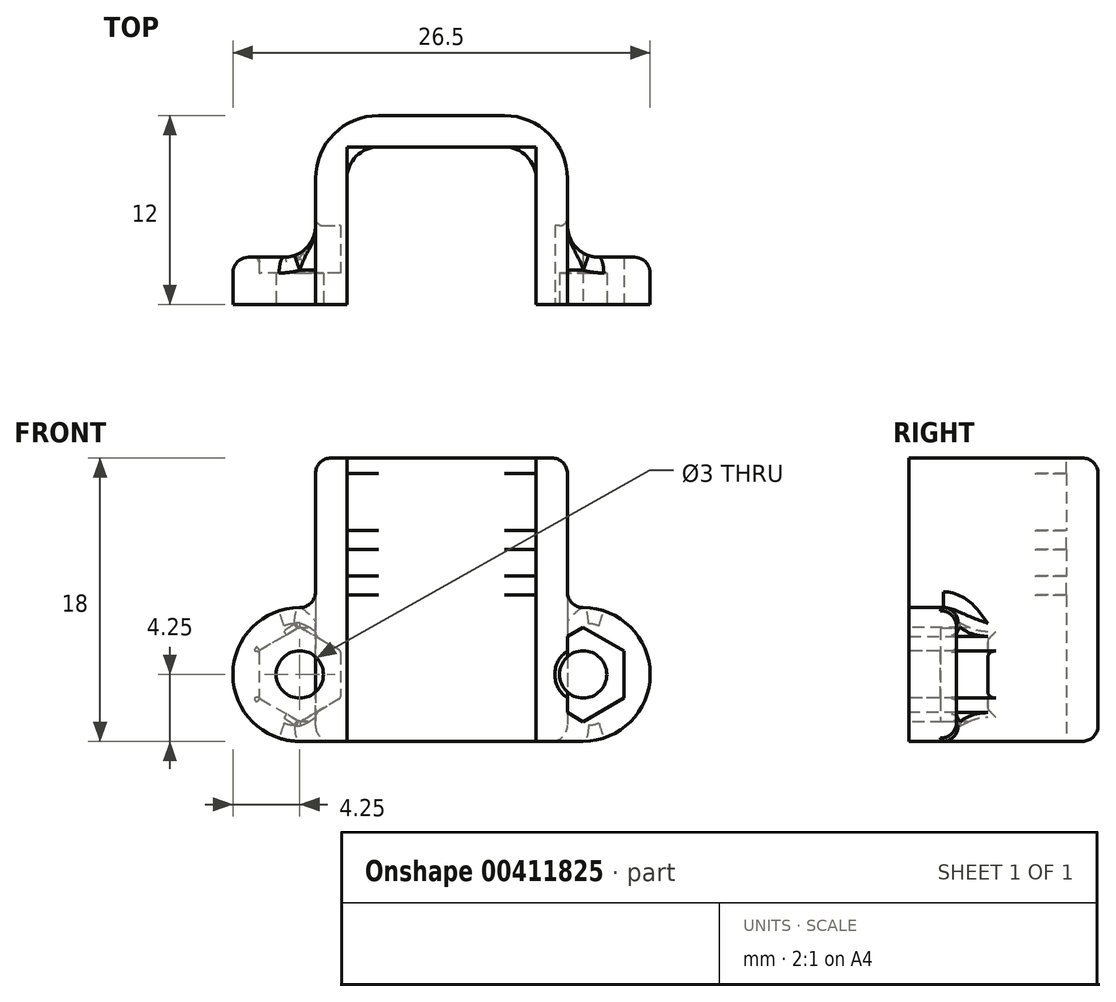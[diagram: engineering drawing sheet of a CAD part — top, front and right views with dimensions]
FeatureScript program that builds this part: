
annotation { "Feature Type Name" : "Feature", "Feature Type Description" : "" }
export const myFeature = defineFeature(function(context is Context, id is Id, definition is map)
    precondition{}
    {
        {
            var Q0;
            Q0=qCreatedBy(makeId("Top.planeOp"),FACE);
            var sketch = newSketch(context, id + "F0", { "sketchPlane" : qUnion([Q0])});
            skLineSegment(sketch, "E0", {"start": v(0, 0) * mm, "end": v(0, 8) * mm});
            skLineSegment(sketch, "E1", {"start": v(2, 10) * mm, "end": v(10, 10) * mm});
            skLineSegment(sketch, "E2", {"start": v(12, 8) * mm, "end": v(12, 0) * mm});
            skLineSegment(sketch, "E3", {"start": v(12, 0) * mm, "end": v(0, 0) * mm, "construction": true});
            skPoint(sketch, "E4.visualSharp", {"position": v(0, 10) * mm});
            skArc(sketch, "E4.filletArc", {"start": v(2, 10) * mm, "mid": v(0.59, 9.41) * mm, "end": v(0, 8) * mm});
            skPoint(sketch, "E5.visualSharp", {"position": v(12, 10) * mm});
            skArc(sketch, "E5.filletArc", {"start": v(12, 8) * mm, "mid": v(11.41, 9.41) * mm, "end": v(10, 10) * mm});
            skLineSegment(sketch, "E6.0", {"start": v(-2, 0) * mm, "end": v(-2, 8) * mm});
            skLineSegment(sketch, "E6.1", {"start": v(14, 8) * mm, "end": v(14, 0) * mm});
            skArc(sketch, "E6.2", {"start": v(14, 8) * mm, "mid": v(12.83, 10.83) * mm, "end": v(10, 12) * mm});
            skLineSegment(sketch, "E6.3", {"start": v(2, 12) * mm, "end": v(10, 12) * mm});
            skArc(sketch, "E6.4", {"start": v(2, 12) * mm, "mid": v(-0.83, 10.83) * mm, "end": v(-2, 8) * mm});
            skLineSegment(sketch, "E7", {"start": v(-2, 0) * mm, "end": v(0, 0) * mm});
            skLineSegment(sketch, "E8", {"start": v(12, 0) * mm, "end": v(14, 0) * mm});
            skSolve(sketch);
        }
        {
            var Q0;
            Q0 = qSketchRegion(id + "F0", true);
            extrude(context, id + "F1", {"entities" : qUnion([Q0]), "depth" : 18 * mm});
        }
        {
            var Q0;
            Q0=qCreatedBy(makeId("Front.planeOp"),FACE);
            var sketch = newSketch(context, id + "F2", { "sketchPlane" : qUnion([Q0])});
            skCircle(sketch, "E9", {"center": v(-3, 4.25) * mm, "radius": 1.8 * mm});
            skCircle(sketch, "E10", {"center": v(-3, 4.25) * mm, "radius": 1.5 * mm});
            skLineSegment(sketch, "E11.bottom", {"start": v(1.25, 8.5) * mm, "end": v(-3, 8.5) * mm, "construction": true});
            skLineSegment(sketch, "E11.top", {"start": v(1.25, 0) * mm, "end": v(-3, 0) * mm, "construction": true});
            skLineSegment(sketch, "E11.left", {"start": v(1.25, 8.5) * mm, "end": v(1.25, 0) * mm, "construction": true});
            skLineSegment(sketch, "E11.right", {"start": v(-7.25, 8.5) * mm, "end": v(-7.25, 0) * mm, "construction": true});
            skLineSegment(sketch, "E12", {"start": v(6, 0) * mm, "end": v(6, 18.17) * mm, "construction": true});
            skLineSegment(sketch, "E13", {"start": v(-3, 0) * mm, "end": v(-7.25, 0) * mm, "construction": true});
            skLineSegment(sketch, "E14", {"start": v(-3, 8.5) * mm, "end": v(-7.25, 8.5) * mm, "construction": true});
            skArc(sketch, "E15", {"start": v(-3, 8.5) * mm, "mid": v(-7.25, 4.25) * mm, "end": v(-3, 0) * mm});
            skArc(sketch, "E16", {"start": v(-3, 0) * mm, "mid": v(1.25, 4.25) * mm, "end": v(-3, 8.5) * mm, "construction": true});
            skLineSegment(sketch, "E17", {"start": v(-3, 0) * mm, "end": v(0, 0) * mm});
            skLineSegment(sketch, "E18", {"start": v(0, 0) * mm, "end": v(0, 8.5) * mm});
            skLineSegment(sketch, "E19", {"start": v(0, 8.5) * mm, "end": v(-3, 8.5) * mm});
            skLineSegment(sketch, "E20.MirrorCS", {"start": v(15, 0) * mm, "end": v(12, 0) * mm});
            skLineSegment(sketch, "E21.MirrorCS", {"start": v(12, 8.5) * mm, "end": v(15, 8.5) * mm});
            skCircle(sketch, "E22.MirrorC", {"center": v(15, 4.25) * mm, "radius": 1.5 * mm});
            skCircle(sketch, "E23.MirrorC", {"center": v(15, 4.25) * mm, "radius": 1.8 * mm});
            skLineSegment(sketch, "E24.MirrorCS", {"start": v(10.75, 8.5) * mm, "end": v(10.75, 0) * mm, "construction": true});
            skLineSegment(sketch, "E25.MirrorCS", {"start": v(15, 8.5) * mm, "end": v(19.25, 8.5) * mm, "construction": true});
            skLineSegment(sketch, "E26.MirrorCS", {"start": v(10.75, 0) * mm, "end": v(15, 0) * mm, "construction": true});
            skArc(sketch, "E27.MirrorCS", {"start": v(15, 0) * mm, "mid": v(10.75, 4.25) * mm, "end": v(15, 8.5) * mm, "construction": true});
            skLineSegment(sketch, "E28.MirrorCS", {"start": v(10.75, 8.5) * mm, "end": v(15, 8.5) * mm, "construction": true});
            skLineSegment(sketch, "E29.MirrorCS", {"start": v(19.25, 8.5) * mm, "end": v(19.25, 0) * mm, "construction": true});
            skLineSegment(sketch, "E30.MirrorCS", {"start": v(15, 0) * mm, "end": v(19.25, 0) * mm, "construction": true});
            skLineSegment(sketch, "E31.MirrorCS", {"start": v(12, 0) * mm, "end": v(12, 8.5) * mm});
            skArc(sketch, "E32.MirrorCS", {"start": v(15, 8.5) * mm, "mid": v(19.25, 4.25) * mm, "end": v(15, 0) * mm});
            skCircle(sketch, "E33", {"center": v(15, 4.25) * mm, "radius": 3 * mm, "construction": true});
            skLineSegment(sketch, "E34.0", {"start": v(17.6, 5.75) * mm, "end": v(17.6, 2.75) * mm});
            skLineSegment(sketch, "E34.1", {"start": v(17.6, 2.75) * mm, "end": v(15, 1.25) * mm});
            skLineSegment(sketch, "E34.2", {"start": v(15, 1.25) * mm, "end": v(12.4, 2.75) * mm});
            skLineSegment(sketch, "E34.3", {"start": v(12.4, 2.75) * mm, "end": v(12.4, 5.75) * mm});
            skLineSegment(sketch, "E34.4", {"start": v(12.4, 5.75) * mm, "end": v(15, 7.25) * mm});
            skLineSegment(sketch, "E34.5", {"start": v(15, 7.25) * mm, "end": v(17.6, 5.75) * mm});
            skLineSegment(sketch, "E35.MirrorCS", {"start": v(-5.6, 5.75) * mm, "end": v(-5.6, 2.75) * mm});
            skLineSegment(sketch, "E36.MirrorCS", {"start": v(-3, 7.25) * mm, "end": v(-5.6, 5.75) * mm});
            skLineSegment(sketch, "E37.MirrorCS", {"start": v(-0.4, 5.75) * mm, "end": v(-3, 7.25) * mm});
            skLineSegment(sketch, "E38.MirrorCS", {"start": v(-0.4, 2.75) * mm, "end": v(-0.4, 5.75) * mm});
            skLineSegment(sketch, "E39.MirrorCS", {"start": v(-3, 1.25) * mm, "end": v(-0.4, 2.75) * mm});
            skLineSegment(sketch, "E40.MirrorCS", {"start": v(-5.6, 2.75) * mm, "end": v(-3, 1.25) * mm});
            skSolve(sketch);
        }
        {
            var Q0;
            Q0=makeQuery(id+"F2.imprint","IMPRINT",FACE,{"disambiguationData":[TD([[makeQuery(id+"F2.imprint","IMPRINT",EDGE,{"derivedFrom":sQuery(id+"F2.wireOp",EDGE,"E9")}),-1.0]])]});
            var Q1;
            Q1=makeQuery(id+"F2.imprint","IMPRINT",FACE,{"disambiguationData":[TD([[makeQuery(id+"F2.imprint","IMPRINT",EDGE,{"derivedFrom":sQuery(id+"F2.wireOp",EDGE,"E9")}),1.0]])]});
            var Q2;
            Q2=makeQuery(id+"F2.imprint","IMPRINT",FACE,{"disambiguationData":[TD([[makeQuery(id+"F2.imprint","IMPRINT",EDGE,{"derivedFrom":sQuery(id+"F2.wireOp",EDGE,"E20.MirrorCS")}),-1.0]])]});
            var Q3;
            Q3=makeQuery(id+"F2.imprint","IMPRINT",FACE,{"disambiguationData":[TD([[makeQuery(id+"F2.imprint","IMPRINT",EDGE,{"derivedFrom":sQuery(id+"F2.wireOp",EDGE,"E22.MirrorC")}),1.0]])]});
            var Q4;
            Q4=makeQuery(id+"F2.imprint","IMPRINT",FACE,{"disambiguationData":[TD([[makeQuery(id+"F2.imprint","IMPRINT",EDGE,{"derivedFrom":sQuery(id+"F2.wireOp",EDGE,"E23.MirrorC")}),1.0]])]});
            var Q5;
            Q5=makeQuery(id+"F2.imprint","IMPRINT",FACE,{"disambiguationData":[TD([[makeQuery(id+"F2.imprint","IMPRINT",EDGE,{"derivedFrom":sQuery(id+"F2.wireOp",EDGE,"E15")}),1.0]])]});
            extrude(context, id + "F3", {"entities" : qUnion([Q0, Q1, Q2, Q3, Q4, Q5]), "operationType" : NewBodyOperationType.ADD, "oppositeDirection" : true, "depth" : 3 * mm});
        }
        {
            var Q0;
            Q0=makeQuery(id+"F2.imprint","IMPRINT",FACE,{"disambiguationData":[TD([[makeQuery(id+"F2.imprint","IMPRINT",EDGE,{"derivedFrom":sQuery(id+"F2.wireOp",EDGE,"E10")}),1.0]])]});
            var Q1;
            Q1=makeQuery(id+"F2.imprint","IMPRINT",FACE,{"disambiguationData":[TD([[makeQuery(id+"F2.imprint","IMPRINT",EDGE,{"derivedFrom":sQuery(id+"F2.wireOp",EDGE,"E22.MirrorC")}),-1.0]])]});
            var Q2;
            Q2=sQuery(id+"F2.wireOp",EDGE,"E10");
            extrude(context, id + "F4", {"entities" : qUnion([Q0, Q1]), "operationType" : NewBodyOperationType.REMOVE, "surfaceEntities" : qUnion([Q2]), "oppositeDirection" : true, "depth" : 5 * mm});
        }
        {
            var Q0;
            Q0=makeQuery(id+"F3.boolean.opBoolean","INTERSECT",EDGE,{"derivedFrom":[makeQuery(id+"F1.opExtrude","SWEPT_FACE",FACE,{"disambiguationData":[OSD([sQuery(id+"F0.wireOp",EDGE,"E6.1")])]}),makeQuery(id+"F3.opExtrude","CAP_FACE",FACE,{"disambiguationData":[OSD([sQuery(id+"F2.wireOp",EDGE,"E20.MirrorCS"),sQuery(id+"F2.wireOp",EDGE,"E21.MirrorCS"),sQuery(id+"F2.wireOp",EDGE,"E22.MirrorC"),sQuery(id+"F2.wireOp",EDGE,"E31.MirrorCS"),sQuery(id+"F2.wireOp",EDGE,"E32.MirrorCS")])],"isStart":false})]});
            var Q1;
            Q1=makeQuery(id+"F3.boolean.opBoolean","INTERSECT",EDGE,{"derivedFrom":[makeQuery(id+"F1.opExtrude","SWEPT_FACE",FACE,{"disambiguationData":[OSD([sQuery(id+"F0.wireOp",EDGE,"E6.0")])]}),makeQuery(id+"F3.opExtrude","CAP_FACE",FACE,{"disambiguationData":[OSD([sQuery(id+"F2.wireOp",EDGE,"E10"),sQuery(id+"F2.wireOp",EDGE,"E15"),sQuery(id+"F2.wireOp",EDGE,"E17"),sQuery(id+"F2.wireOp",EDGE,"E18"),sQuery(id+"F2.wireOp",EDGE,"E19")])],"isStart":false})]});
            fillet(context, id + "F5", {"entities" : qUnion([Q0, Q1]), "radius" : 2 * mm, "tangentPropagation" : true, "allowEdgeOverflow" : false});
        }
        {
            var Q0;
            Q0=makeQuery(id+"F3.opExtrude","CAP_EDGE",EDGE,{"disambiguationData":[OSD([sQuery(id+"F2.wireOp",EDGE,"E15")])],"isStart":false});
            var Q1;
            Q1=makeQuery(id+"F3.opExtrude","CAP_EDGE",EDGE,{"disambiguationData":[OSD([sQuery(id+"F2.wireOp",EDGE,"E32.MirrorCS")])],"isStart":false});
            fillet(context, id + "F6", {"entities" : qUnion([Q0, Q1]), "radius" : 1 * mm, "tangentPropagation" : true, "allowEdgeOverflow" : false});
        }
        {
            var Q0;
            Q0=makeQuery(id+"F1.opExtrude","CAP_EDGE",EDGE,{"disambiguationData":[OSD([sQuery(id+"F0.wireOp",EDGE,"E6.3")])],"isStart":false});
            var Q1;
            Q1=makeQuery(id+"F1.opExtrude","CAP_EDGE",EDGE,{"disambiguationData":[OSD([sQuery(id+"F0.wireOp",EDGE,"E6.2")])],"isStart":false});
            var Q2;
            Q2=makeQuery(id+"F1.opExtrude","CAP_EDGE",EDGE,{"disambiguationData":[OSD([sQuery(id+"F0.wireOp",EDGE,"E6.1")])],"isStart":false});
            var Q3;
            Q3=makeQuery(id+"F1.opExtrude","CAP_EDGE",EDGE,{"disambiguationData":[OSD([sQuery(id+"F0.wireOp",EDGE,"E6.4")])],"isStart":false});
            var Q4;
            Q4=makeQuery(id+"F1.opExtrude","CAP_EDGE",EDGE,{"disambiguationData":[OSD([sQuery(id+"F0.wireOp",EDGE,"E6.0")])],"isStart":false});
            fillet(context, id + "F7", {"entities" : qUnion([Q0, Q1, Q2, Q3, Q4]), "radius" : 1 * mm, "tangentPropagation" : true, "allowEdgeOverflow" : false});
        }
        {
            var Q0;
            {var subQ0=makeQuery(id+"F1.opExtrude","SWEPT_FACE",FACE,{"disambiguationData":[OSD([sQuery(id+"F0.wireOp",EDGE,"E6.1")])]});var subQ1=sQuery(id+"F2.wireOp",EDGE,"E21.MirrorCS");Q0=makeQuery(id+"F6.opFillet","BLEND_EDGE",EDGE,{"blendedFrom":[makeQuery(id+"F5.opFillet","BLEND_EDGE",EDGE,{"blendedFrom":[makeQuery(id+"F3.boolean.opBoolean","INTERSECT",EDGE,{"derivedFrom":[subQ0,makeQuery(id+"F3.opExtrude","CAP_FACE",FACE,{"disambiguationData":[OSD([sQuery(id+"F2.wireOp",EDGE,"E20.MirrorCS"),subQ1,sQuery(id+"F2.wireOp",EDGE,"E22.MirrorC"),sQuery(id+"F2.wireOp",EDGE,"E31.MirrorCS"),sQuery(id+"F2.wireOp",EDGE,"E32.MirrorCS")])],"isStart":false})]}),makeQuery(id+"F3.opExtrude","SWEPT_FACE",FACE,{"disambiguationData":[OSD([subQ1])]})],"blendedInto":[makeQuery(id+"F3.opExtrude","SWEPT_FACE",FACE,{"disambiguationData":[OSD([subQ1])]})]}),subQ0],"blendedInto":[subQ0]});}
            var Q1;
            Q1=makeQuery(id+"F3.boolean.opBoolean","INTERSECT",EDGE,{"derivedFrom":[makeQuery(id+"F1.opExtrude","SWEPT_FACE",FACE,{"disambiguationData":[OSD([sQuery(id+"F0.wireOp",EDGE,"E6.1")])]}),makeQuery(id+"F3.opExtrude","SWEPT_FACE",FACE,{"disambiguationData":[OSD([sQuery(id+"F2.wireOp",EDGE,"E21.MirrorCS")])]})]});
            var Q2;
            {var subQ0=makeQuery(id+"F1.opExtrude","SWEPT_FACE",FACE,{"disambiguationData":[OSD([sQuery(id+"F0.wireOp",EDGE,"E6.0")])]});var subQ1=sQuery(id+"F2.wireOp",EDGE,"E19");Q2=makeQuery(id+"F6.opFillet","BLEND_EDGE",EDGE,{"blendedFrom":[makeQuery(id+"F5.opFillet","BLEND_EDGE",EDGE,{"blendedFrom":[makeQuery(id+"F3.boolean.opBoolean","INTERSECT",EDGE,{"derivedFrom":[subQ0,makeQuery(id+"F3.opExtrude","CAP_FACE",FACE,{"disambiguationData":[OSD([sQuery(id+"F2.wireOp",EDGE,"E10"),sQuery(id+"F2.wireOp",EDGE,"E15"),sQuery(id+"F2.wireOp",EDGE,"E17"),sQuery(id+"F2.wireOp",EDGE,"E18"),subQ1])],"isStart":false})]}),makeQuery(id+"F3.opExtrude","SWEPT_FACE",FACE,{"disambiguationData":[OSD([subQ1])]})],"blendedInto":[makeQuery(id+"F3.opExtrude","SWEPT_FACE",FACE,{"disambiguationData":[OSD([subQ1])]})]}),subQ0],"blendedInto":[subQ0]});}
            var Q3;
            Q3=makeQuery(id+"F3.boolean.opBoolean","INTERSECT",EDGE,{"derivedFrom":[makeQuery(id+"F1.opExtrude","SWEPT_FACE",FACE,{"disambiguationData":[OSD([sQuery(id+"F0.wireOp",EDGE,"E6.0")])]}),makeQuery(id+"F3.opExtrude","SWEPT_FACE",FACE,{"disambiguationData":[OSD([sQuery(id+"F2.wireOp",EDGE,"E19")])]})]});
            fillet(context, id + "F8", {"entities" : qUnion([Q0, Q1, Q2, Q3]), "radius" : 1 * mm, "tangentPropagation" : true, "allowEdgeOverflow" : false});
        }
        {
            var Q0;
            Q0=makeQuery(id+"F2.imprint","IMPRINT",FACE,{"disambiguationData":[TD([[makeQuery(id+"F2.imprint","IMPRINT",EDGE,{"derivedFrom":sQuery(id+"F2.wireOp",EDGE,"E23.MirrorC")}),1.0]])]});
            var Q1;
            Q1=makeQuery(id+"F2.imprint","IMPRINT",FACE,{"disambiguationData":[TD([[makeQuery(id+"F2.imprint","IMPRINT",EDGE,{"derivedFrom":sQuery(id+"F2.wireOp",EDGE,"E22.MirrorC")}),1.0]])]});
            var Q2;
            Q2=makeQuery(id+"F2.imprint","IMPRINT",FACE,{"disambiguationData":[TD([[makeQuery(id+"F2.imprint","IMPRINT",EDGE,{"derivedFrom":sQuery(id+"F2.wireOp",EDGE,"E9")}),-1.0]])]});
            var Q3;
            Q3=makeQuery(id+"F2.imprint","IMPRINT",FACE,{"disambiguationData":[TD([[makeQuery(id+"F2.imprint","IMPRINT",EDGE,{"derivedFrom":sQuery(id+"F2.wireOp",EDGE,"E9")}),1.0]])]});
            var Q4;
            Q4=makeQuery(id+"F4.boolean.opBoolean","COPY",FACE,{"derivedFrom":makeQuery(id+"F4.opExtrude","CAP_FACE",FACE,{"disambiguationData":[OSD([sQuery(id+"F2.wireOp",EDGE,"E10")])],"isStart":false})});
            extrude(context, id + "F9", {"entities" : qUnion([Q0, Q1, Q2, Q3]), "operationType" : NewBodyOperationType.REMOVE, "endBound" : BoundingType.UP_TO_SURFACE, "oppositeDirection" : true, "endBoundEntityFace" : qUnion([Q4]), "depth" : 4 * mm, "hasSecondDirection" : true, "secondDirectionOppositeDirection" : true, "secondDirectionDepth" : 2 * mm});
        }
        {
            var Q0;
            Q0=qCreatedBy(makeId("Front.planeOp"),FACE);
            var sketch = newSketch(context, id + "F10", { "sketchPlane" : qUnion([Q0])});
            skLineSegment(sketch, "E41.bottom", {"start": v(0, 0) * mm, "end": v(12, 0) * mm, "construction": true});
            skLineSegment(sketch, "E41.top", {"start": v(0, 18) * mm, "end": v(12, 18) * mm, "construction": true});
            skLineSegment(sketch, "E41.left", {"start": v(0, 0) * mm, "end": v(0, 18) * mm, "construction": true});
            skLineSegment(sketch, "E41.right", {"start": v(12, 0) * mm, "end": v(12, 18) * mm, "construction": true});
            skPoint(sketch, "E42", {"position": v(0, 17.6) * mm});
            skPoint(sketch, "E43", {"position": v(0, 12.8) * mm});
            skPoint(sketch, "E44", {"position": v(0, 9.9) * mm});
            skLineSegment(sketch, "E45.bottom", {"start": v(0, 17) * mm, "end": v(12, 17) * mm});
            skLineSegment(sketch, "E45.top", {"start": v(0, 18.2) * mm, "end": v(12, 18.2) * mm});
            skLineSegment(sketch, "E45.left", {"start": v(0, 17) * mm, "end": v(0, 18.2) * mm});
            skLineSegment(sketch, "E45.right", {"start": v(12, 17) * mm, "end": v(12, 18.2) * mm});
            skLineSegment(sketch, "E46.bottom", {"start": v(0, 12.2) * mm, "end": v(12, 12.2) * mm});
            skLineSegment(sketch, "E46.top", {"start": v(0, 13.4) * mm, "end": v(12, 13.4) * mm});
            skLineSegment(sketch, "E46.left", {"start": v(0, 12.2) * mm, "end": v(0, 13.4) * mm});
            skLineSegment(sketch, "E46.right", {"start": v(12, 12.2) * mm, "end": v(12, 13.4) * mm});
            skLineSegment(sketch, "E47.bottom", {"start": v(0, 9.3) * mm, "end": v(12, 9.3) * mm});
            skLineSegment(sketch, "E47.top", {"start": v(0, 10.5) * mm, "end": v(12, 10.5) * mm});
            skLineSegment(sketch, "E47.left", {"start": v(0, 9.3) * mm, "end": v(0, 10.5) * mm});
            skLineSegment(sketch, "E47.right", {"start": v(12, 9.3) * mm, "end": v(12, 10.5) * mm});
            skSolve(sketch);
        }
        {
            var Q0;
            Q0 = qSketchRegion(id + "F10", true);
            var Q1;
            Q1=makeQuery(id+"F1.opExtrude","SWEPT_FACE",FACE,{"disambiguationData":[OSD([sQuery(id+"F0.wireOp",EDGE,"E1")])]});
            extrude(context, id + "F11", {"entities" : qUnion([Q0]), "operationType" : NewBodyOperationType.REMOVE, "endBound" : BoundingType.UP_TO_SURFACE, "oppositeDirection" : true, "endBoundEntityFace" : qUnion([Q1]), "depth" : 25 * mm});
        }
        {
            var Q0;
            {var subQ0=makeQuery(id+"F1.opExtrude","SWEPT_FACE",FACE,{"disambiguationData":[OSD([sQuery(id+"F0.wireOp",EDGE,"E6.0")])]});var subQ1=subQ0;var subQ2=subQ1;var subQ3=sQuery(id+"F2.wireOp",EDGE,"E10");var subQ4=makeQuery(id+"F3.opExtrude","CAP_FACE",FACE,{"disambiguationData":[OSD([subQ3,sQuery(id+"F2.wireOp",EDGE,"E15"),sQuery(id+"F2.wireOp",EDGE,"E17"),sQuery(id+"F2.wireOp",EDGE,"E18"),sQuery(id+"F2.wireOp",EDGE,"E19")])],"isStart":false});Q0=makeQuery(id+"F9.boolean.opBoolean","MERGE",EDGE,{"derivedFrom":[makeQuery(id+"F4.boolean.opBoolean","INTERSECT",EDGE,{"derivedFrom":[subQ1,makeQuery(id+"F4.opExtrude","CAP_FACE",FACE,{"disambiguationData":[OSD([subQ3])],"isStart":false})]}),makeQuery(id+"F5.opFillet","BLEND_EDGE",EDGE,{"blendedFrom":[makeQuery(id+"F3.boolean.opBoolean","INTERSECT",EDGE,{"disambiguationData":[OD(0.0)],"derivedFrom":[subQ0,subQ4]}),subQ2],"blendedInto":[subQ2]}),makeQuery(id+"F5.opFillet","BLEND_EDGE",EDGE,{"blendedFrom":[makeQuery(id+"F3.boolean.opBoolean","INTERSECT",EDGE,{"disambiguationData":[OD(1.0)],"derivedFrom":[subQ0,subQ4]}),subQ2],"blendedInto":[subQ2]})]});}
            var Q1;
            {var subQ0=sQuery(id+"F2.wireOp",EDGE,"E19");var subQ1=sQuery(id+"F2.wireOp",EDGE,"E18");var subQ2=sQuery(id+"F2.wireOp",EDGE,"E17");var subQ3=sQuery(id+"F2.wireOp",EDGE,"E15");var subQ4=sQuery(id+"F2.wireOp",EDGE,"E10");var subQ5=sQuery(id+"F0.wireOp",EDGE,"E6.0");Q1=makeQuery(id+"F9.boolean.opBoolean","INTERSECT",EDGE,{"derivedFrom":[makeQuery(id+"F5.opFillet","BLEND_FACE",FACE,{"disambiguationData":[OSD([subQ5,subQ4,subQ3,subQ2,subQ1,subQ0]),TDD([makeQuery(id+"F3.boolean.opBoolean","INTERSECT",EDGE,{"disambiguationData":[OD(0.0)],"derivedFrom":[makeQuery(id+"F1.opExtrude","SWEPT_FACE",FACE,{"disambiguationData":[OSD([subQ5])]}),makeQuery(id+"F3.opExtrude","CAP_FACE",FACE,{"disambiguationData":[OSD([subQ4,subQ3,subQ2,subQ1,subQ0])],"isStart":false})]})])]}),makeQuery(id+"F9.opExtrude","SWEPT_FACE",FACE,{"disambiguationData":[OSD([sQuery(id+"F2.wireOp",EDGE,"E39.MirrorCS")])]})]});}
            var Q2;
            {var subQ0=sQuery(id+"F2.wireOp",EDGE,"E19");var subQ1=sQuery(id+"F2.wireOp",EDGE,"E18");var subQ2=sQuery(id+"F2.wireOp",EDGE,"E17");var subQ3=sQuery(id+"F2.wireOp",EDGE,"E15");var subQ4=sQuery(id+"F2.wireOp",EDGE,"E10");var subQ5=sQuery(id+"F0.wireOp",EDGE,"E6.0");Q2=makeQuery(id+"F9.boolean.opBoolean","INTERSECT",EDGE,{"derivedFrom":[makeQuery(id+"F5.opFillet","BLEND_FACE",FACE,{"disambiguationData":[OSD([subQ5,subQ4,subQ3,subQ2,subQ1,subQ0]),TDD([makeQuery(id+"F3.boolean.opBoolean","INTERSECT",EDGE,{"disambiguationData":[OD(1.0)],"derivedFrom":[makeQuery(id+"F1.opExtrude","SWEPT_FACE",FACE,{"disambiguationData":[OSD([subQ5])]}),makeQuery(id+"F3.opExtrude","CAP_FACE",FACE,{"disambiguationData":[OSD([subQ4,subQ3,subQ2,subQ1,subQ0])],"isStart":false})]})])]}),makeQuery(id+"F9.opExtrude","SWEPT_FACE",FACE,{"disambiguationData":[OSD([sQuery(id+"F2.wireOp",EDGE,"E37.MirrorCS")])]})]});}
            var Q3;
            {var subQ0=sQuery(id+"F2.wireOp",EDGE,"E32.MirrorCS");var subQ1=sQuery(id+"F2.wireOp",EDGE,"E31.MirrorCS");var subQ2=sQuery(id+"F2.wireOp",EDGE,"E22.MirrorC");var subQ3=sQuery(id+"F2.wireOp",EDGE,"E21.MirrorCS");var subQ4=sQuery(id+"F2.wireOp",EDGE,"E20.MirrorCS");var subQ5=sQuery(id+"F0.wireOp",EDGE,"E6.1");Q3=makeQuery(id+"F9.boolean.opBoolean","INTERSECT",EDGE,{"derivedFrom":[makeQuery(id+"F5.opFillet","BLEND_FACE",FACE,{"disambiguationData":[OSD([subQ5,subQ4,subQ3,subQ2,subQ1,subQ0]),TDD([makeQuery(id+"F3.boolean.opBoolean","INTERSECT",EDGE,{"disambiguationData":[OD(0.0)],"derivedFrom":[makeQuery(id+"F1.opExtrude","SWEPT_FACE",FACE,{"disambiguationData":[OSD([subQ5])]}),makeQuery(id+"F3.opExtrude","CAP_FACE",FACE,{"disambiguationData":[OSD([subQ4,subQ3,subQ2,subQ1,subQ0])],"isStart":false})]})])]}),makeQuery(id+"F9.opExtrude","SWEPT_FACE",FACE,{"disambiguationData":[OSD([sQuery(id+"F2.wireOp",EDGE,"E34.2")])]})]});}
            var Q4;
            {var subQ0=makeQuery(id+"F1.opExtrude","SWEPT_FACE",FACE,{"disambiguationData":[OSD([sQuery(id+"F0.wireOp",EDGE,"E6.1")])]});var subQ1=subQ0;var subQ2=subQ1;var subQ3=sQuery(id+"F2.wireOp",EDGE,"E22.MirrorC");var subQ4=makeQuery(id+"F3.opExtrude","CAP_FACE",FACE,{"disambiguationData":[OSD([sQuery(id+"F2.wireOp",EDGE,"E20.MirrorCS"),sQuery(id+"F2.wireOp",EDGE,"E21.MirrorCS"),subQ3,sQuery(id+"F2.wireOp",EDGE,"E31.MirrorCS"),sQuery(id+"F2.wireOp",EDGE,"E32.MirrorCS")])],"isStart":false});Q4=makeQuery(id+"F9.boolean.opBoolean","MERGE",EDGE,{"derivedFrom":[makeQuery(id+"F4.boolean.opBoolean","INTERSECT",EDGE,{"derivedFrom":[subQ1,makeQuery(id+"F4.opExtrude","CAP_FACE",FACE,{"disambiguationData":[OSD([subQ3])],"isStart":false})]}),makeQuery(id+"F5.opFillet","BLEND_EDGE",EDGE,{"blendedFrom":[makeQuery(id+"F3.boolean.opBoolean","INTERSECT",EDGE,{"disambiguationData":[OD(1.0)],"derivedFrom":[subQ0,subQ4]}),subQ2],"blendedInto":[subQ2]}),makeQuery(id+"F5.opFillet","BLEND_EDGE",EDGE,{"blendedFrom":[makeQuery(id+"F3.boolean.opBoolean","INTERSECT",EDGE,{"disambiguationData":[OD(0.0)],"derivedFrom":[subQ0,subQ4]}),subQ2],"blendedInto":[subQ2]})]});}
            var Q5;
            {var subQ0=sQuery(id+"F2.wireOp",EDGE,"E32.MirrorCS");var subQ1=sQuery(id+"F2.wireOp",EDGE,"E31.MirrorCS");var subQ2=sQuery(id+"F2.wireOp",EDGE,"E22.MirrorC");var subQ3=sQuery(id+"F2.wireOp",EDGE,"E21.MirrorCS");var subQ4=sQuery(id+"F2.wireOp",EDGE,"E20.MirrorCS");var subQ5=sQuery(id+"F0.wireOp",EDGE,"E6.1");Q5=makeQuery(id+"F9.boolean.opBoolean","INTERSECT",EDGE,{"derivedFrom":[makeQuery(id+"F5.opFillet","BLEND_FACE",FACE,{"disambiguationData":[OSD([subQ5,subQ4,subQ3,subQ2,subQ1,subQ0]),TDD([makeQuery(id+"F3.boolean.opBoolean","INTERSECT",EDGE,{"disambiguationData":[OD(1.0)],"derivedFrom":[makeQuery(id+"F1.opExtrude","SWEPT_FACE",FACE,{"disambiguationData":[OSD([subQ5])]}),makeQuery(id+"F3.opExtrude","CAP_FACE",FACE,{"disambiguationData":[OSD([subQ4,subQ3,subQ2,subQ1,subQ0])],"isStart":false})]})])]}),makeQuery(id+"F9.opExtrude","SWEPT_FACE",FACE,{"disambiguationData":[OSD([sQuery(id+"F2.wireOp",EDGE,"E34.4")])]})]});}
            fillet(context, id + "F12", {"entities" : qUnion([Q0, Q1, Q2, Q3, Q4, Q5]), "radius" : 0.5 * mm, "tangentPropagation" : true, "allowEdgeOverflow" : false});
        }
        {
            var Q0;
            Q0=makeQuery(id+"F9.boolean.opBoolean","COPY",EDGE,{"derivedFrom":makeQuery(id+"F9.opExtrude","SWEPT_EDGE",EDGE,{"disambiguationData":[OSD([sQuery(id+"F2.wireOp",EDGE,"E34.2"),sQuery(id+"F2.wireOp",EDGE,"E34.3")])]})});
            var Q1;
            Q1=makeQuery(id+"F9.boolean.opBoolean","COPY",EDGE,{"derivedFrom":makeQuery(id+"F9.opExtrude","SWEPT_EDGE",EDGE,{"disambiguationData":[OSD([sQuery(id+"F2.wireOp",EDGE,"E34.3"),sQuery(id+"F2.wireOp",EDGE,"E34.4")])]})});
            var Q2;
            Q2=makeQuery(id+"F9.boolean.opBoolean","COPY",EDGE,{"derivedFrom":makeQuery(id+"F9.opExtrude","SWEPT_EDGE",EDGE,{"disambiguationData":[OSD([sQuery(id+"F2.wireOp",EDGE,"E38.MirrorCS"),sQuery(id+"F2.wireOp",EDGE,"E39.MirrorCS")])]})});
            var Q3;
            Q3=makeQuery(id+"F9.boolean.opBoolean","COPY",EDGE,{"derivedFrom":makeQuery(id+"F9.opExtrude","SWEPT_EDGE",EDGE,{"disambiguationData":[OSD([sQuery(id+"F2.wireOp",EDGE,"E37.MirrorCS"),sQuery(id+"F2.wireOp",EDGE,"E38.MirrorCS")])]})});
            var Q4;
            {var subQ0=sQuery(id+"F2.wireOp",EDGE,"E19");var subQ1=sQuery(id+"F2.wireOp",EDGE,"E18");var subQ2=sQuery(id+"F2.wireOp",EDGE,"E17");var subQ3=sQuery(id+"F2.wireOp",EDGE,"E15");var subQ4=sQuery(id+"F2.wireOp",EDGE,"E10");var subQ5=sQuery(id+"F0.wireOp",EDGE,"E6.0");Q4=makeQuery(id+"F12.opFillet","BLEND_EDGE",EDGE,{"blendedFrom":[makeQuery(id+"F9.boolean.opBoolean","INTERSECT",EDGE,{"derivedFrom":[makeQuery(id+"F5.opFillet","BLEND_FACE",FACE,{"disambiguationData":[OSD([subQ5,subQ4,subQ3,subQ2,subQ1,subQ0]),TDD([makeQuery(id+"F3.boolean.opBoolean","INTERSECT",EDGE,{"disambiguationData":[OD(0.0)],"derivedFrom":[makeQuery(id+"F1.opExtrude","SWEPT_FACE",FACE,{"disambiguationData":[OSD([subQ5])]}),makeQuery(id+"F3.opExtrude","CAP_FACE",FACE,{"disambiguationData":[OSD([subQ4,subQ3,subQ2,subQ1,subQ0])],"isStart":false})]})])]}),makeQuery(id+"F9.opExtrude","SWEPT_FACE",FACE,{"disambiguationData":[OSD([sQuery(id+"F2.wireOp",EDGE,"E39.MirrorCS")])]})]}),makeQuery(id+"F9.boolean.opBoolean","COPY",FACE,{"derivedFrom":makeQuery(id+"F9.opExtrude","SWEPT_FACE",FACE,{"disambiguationData":[OSD([sQuery(id+"F2.wireOp",EDGE,"E40.MirrorCS")])]})})],"blendedInto":[makeQuery(id+"F9.boolean.opBoolean","COPY",FACE,{"derivedFrom":makeQuery(id+"F9.opExtrude","SWEPT_FACE",FACE,{"disambiguationData":[OSD([sQuery(id+"F2.wireOp",EDGE,"E40.MirrorCS")])]})})]});}
            var Q5;
            {var subQ0=sQuery(id+"F2.wireOp",EDGE,"E19");var subQ1=sQuery(id+"F2.wireOp",EDGE,"E18");var subQ2=sQuery(id+"F2.wireOp",EDGE,"E17");var subQ3=sQuery(id+"F2.wireOp",EDGE,"E15");var subQ4=sQuery(id+"F2.wireOp",EDGE,"E10");var subQ5=sQuery(id+"F0.wireOp",EDGE,"E6.0");Q5=makeQuery(id+"F12.opFillet","BLEND_EDGE",EDGE,{"blendedFrom":[makeQuery(id+"F9.boolean.opBoolean","INTERSECT",EDGE,{"derivedFrom":[makeQuery(id+"F5.opFillet","BLEND_FACE",FACE,{"disambiguationData":[OSD([subQ5,subQ4,subQ3,subQ2,subQ1,subQ0]),TDD([makeQuery(id+"F3.boolean.opBoolean","INTERSECT",EDGE,{"disambiguationData":[OD(1.0)],"derivedFrom":[makeQuery(id+"F1.opExtrude","SWEPT_FACE",FACE,{"disambiguationData":[OSD([subQ5])]}),makeQuery(id+"F3.opExtrude","CAP_FACE",FACE,{"disambiguationData":[OSD([subQ4,subQ3,subQ2,subQ1,subQ0])],"isStart":false})]})])]}),makeQuery(id+"F9.opExtrude","SWEPT_FACE",FACE,{"disambiguationData":[OSD([sQuery(id+"F2.wireOp",EDGE,"E37.MirrorCS")])]})]}),makeQuery(id+"F9.boolean.opBoolean","COPY",FACE,{"derivedFrom":makeQuery(id+"F9.opExtrude","SWEPT_FACE",FACE,{"disambiguationData":[OSD([sQuery(id+"F2.wireOp",EDGE,"E36.MirrorCS")])]})})],"blendedInto":[makeQuery(id+"F9.boolean.opBoolean","COPY",FACE,{"derivedFrom":makeQuery(id+"F9.opExtrude","SWEPT_FACE",FACE,{"disambiguationData":[OSD([sQuery(id+"F2.wireOp",EDGE,"E36.MirrorCS")])]})})]});}
            var Q6;
            {var subQ0=sQuery(id+"F2.wireOp",EDGE,"E32.MirrorCS");var subQ1=sQuery(id+"F2.wireOp",EDGE,"E31.MirrorCS");var subQ2=sQuery(id+"F2.wireOp",EDGE,"E22.MirrorC");var subQ3=sQuery(id+"F2.wireOp",EDGE,"E21.MirrorCS");var subQ4=sQuery(id+"F2.wireOp",EDGE,"E20.MirrorCS");var subQ5=sQuery(id+"F0.wireOp",EDGE,"E6.1");Q6=makeQuery(id+"F12.opFillet","BLEND_EDGE",EDGE,{"blendedFrom":[makeQuery(id+"F9.boolean.opBoolean","INTERSECT",EDGE,{"derivedFrom":[makeQuery(id+"F5.opFillet","BLEND_FACE",FACE,{"disambiguationData":[OSD([subQ5,subQ4,subQ3,subQ2,subQ1,subQ0]),TDD([makeQuery(id+"F3.boolean.opBoolean","INTERSECT",EDGE,{"disambiguationData":[OD(1.0)],"derivedFrom":[makeQuery(id+"F1.opExtrude","SWEPT_FACE",FACE,{"disambiguationData":[OSD([subQ5])]}),makeQuery(id+"F3.opExtrude","CAP_FACE",FACE,{"disambiguationData":[OSD([subQ4,subQ3,subQ2,subQ1,subQ0])],"isStart":false})]})])]}),makeQuery(id+"F9.opExtrude","SWEPT_FACE",FACE,{"disambiguationData":[OSD([sQuery(id+"F2.wireOp",EDGE,"E34.4")])]})]}),makeQuery(id+"F9.boolean.opBoolean","COPY",FACE,{"derivedFrom":makeQuery(id+"F9.opExtrude","SWEPT_FACE",FACE,{"disambiguationData":[OSD([sQuery(id+"F2.wireOp",EDGE,"E34.5")])]})})],"blendedInto":[makeQuery(id+"F9.boolean.opBoolean","COPY",FACE,{"derivedFrom":makeQuery(id+"F9.opExtrude","SWEPT_FACE",FACE,{"disambiguationData":[OSD([sQuery(id+"F2.wireOp",EDGE,"E34.5")])]})})]});}
            var Q7;
            {var subQ0=sQuery(id+"F2.wireOp",EDGE,"E32.MirrorCS");var subQ1=sQuery(id+"F2.wireOp",EDGE,"E31.MirrorCS");var subQ2=sQuery(id+"F2.wireOp",EDGE,"E22.MirrorC");var subQ3=sQuery(id+"F2.wireOp",EDGE,"E21.MirrorCS");var subQ4=sQuery(id+"F2.wireOp",EDGE,"E20.MirrorCS");var subQ5=sQuery(id+"F0.wireOp",EDGE,"E6.1");Q7=makeQuery(id+"F12.opFillet","BLEND_EDGE",EDGE,{"blendedFrom":[makeQuery(id+"F9.boolean.opBoolean","INTERSECT",EDGE,{"derivedFrom":[makeQuery(id+"F5.opFillet","BLEND_FACE",FACE,{"disambiguationData":[OSD([subQ5,subQ4,subQ3,subQ2,subQ1,subQ0]),TDD([makeQuery(id+"F3.boolean.opBoolean","INTERSECT",EDGE,{"disambiguationData":[OD(0.0)],"derivedFrom":[makeQuery(id+"F1.opExtrude","SWEPT_FACE",FACE,{"disambiguationData":[OSD([subQ5])]}),makeQuery(id+"F3.opExtrude","CAP_FACE",FACE,{"disambiguationData":[OSD([subQ4,subQ3,subQ2,subQ1,subQ0])],"isStart":false})]})])]}),makeQuery(id+"F9.opExtrude","SWEPT_FACE",FACE,{"disambiguationData":[OSD([sQuery(id+"F2.wireOp",EDGE,"E34.2")])]})]}),makeQuery(id+"F9.boolean.opBoolean","COPY",FACE,{"derivedFrom":makeQuery(id+"F9.opExtrude","SWEPT_FACE",FACE,{"disambiguationData":[OSD([sQuery(id+"F2.wireOp",EDGE,"E34.1")])]})})],"blendedInto":[makeQuery(id+"F9.boolean.opBoolean","COPY",FACE,{"derivedFrom":makeQuery(id+"F9.opExtrude","SWEPT_FACE",FACE,{"disambiguationData":[OSD([sQuery(id+"F2.wireOp",EDGE,"E34.1")])]})})]});}
            var Q8;
            Q8=makeQuery(id+"F9.boolean.opBoolean","COPY",EDGE,{"derivedFrom":makeQuery(id+"F9.opExtrude","SWEPT_EDGE",EDGE,{"disambiguationData":[OSD([sQuery(id+"F2.wireOp",EDGE,"E34.0"),sQuery(id+"F2.wireOp",EDGE,"E34.1")])]})});
            var Q9;
            Q9=makeQuery(id+"F9.boolean.opBoolean","COPY",EDGE,{"derivedFrom":makeQuery(id+"F9.opExtrude","SWEPT_EDGE",EDGE,{"disambiguationData":[OSD([sQuery(id+"F2.wireOp",EDGE,"E34.0"),sQuery(id+"F2.wireOp",EDGE,"E34.5")])]})});
            var Q10;
            Q10=makeQuery(id+"F9.boolean.opBoolean","COPY",EDGE,{"derivedFrom":makeQuery(id+"F9.opExtrude","SWEPT_EDGE",EDGE,{"disambiguationData":[OSD([sQuery(id+"F2.wireOp",EDGE,"E35.MirrorCS"),sQuery(id+"F2.wireOp",EDGE,"E36.MirrorCS")])]})});
            var Q11;
            Q11=makeQuery(id+"F9.boolean.opBoolean","COPY",EDGE,{"derivedFrom":makeQuery(id+"F9.opExtrude","SWEPT_EDGE",EDGE,{"disambiguationData":[OSD([sQuery(id+"F2.wireOp",EDGE,"E35.MirrorCS"),sQuery(id+"F2.wireOp",EDGE,"E40.MirrorCS")])]})});
            fillet(context, id + "F13", {"entities" : qUnion([Q0, Q1, Q2, Q3, Q4, Q5, Q6, Q7, Q8, Q9, Q10, Q11]), "radius" : 0.2 * mm, "tangentPropagation" : true, "allowEdgeOverflow" : false});
        }
        {
            var Q0;
            Q0=makeQuery(id+"F9.boolean.opBoolean","INTERSECT",EDGE,{"derivedFrom":[makeQuery(id+"F1.opExtrude","SWEPT_FACE",FACE,{"disambiguationData":[OSD([sQuery(id+"F0.wireOp",EDGE,"E6.4")])]}),makeQuery(id+"F9.opExtrude","SWEPT_FACE",FACE,{"disambiguationData":[OSD([sQuery(id+"F2.wireOp",EDGE,"E39.MirrorCS")])]})]});
            var Q1;
            Q1=makeQuery(id+"F9.boolean.opBoolean","INTERSECT",EDGE,{"derivedFrom":[makeQuery(id+"F1.opExtrude","SWEPT_FACE",FACE,{"disambiguationData":[OSD([sQuery(id+"F0.wireOp",EDGE,"E6.4")])]}),makeQuery(id+"F9.opExtrude","SWEPT_FACE",FACE,{"disambiguationData":[OSD([sQuery(id+"F2.wireOp",EDGE,"E38.MirrorCS")])]})]});
            var Q2;
            Q2=makeQuery(id+"F9.boolean.opBoolean","INTERSECT",EDGE,{"derivedFrom":[makeQuery(id+"F1.opExtrude","SWEPT_FACE",FACE,{"disambiguationData":[OSD([sQuery(id+"F0.wireOp",EDGE,"E6.4")])]}),makeQuery(id+"F9.opExtrude","SWEPT_FACE",FACE,{"disambiguationData":[OSD([sQuery(id+"F2.wireOp",EDGE,"E37.MirrorCS")])]})]});
            var Q3;
            {var subQ0=sQuery(id+"F2.wireOp",EDGE,"E19");var subQ1=sQuery(id+"F2.wireOp",EDGE,"E18");var subQ2=sQuery(id+"F2.wireOp",EDGE,"E17");var subQ3=sQuery(id+"F2.wireOp",EDGE,"E15");var subQ4=sQuery(id+"F2.wireOp",EDGE,"E10");var subQ5=sQuery(id+"F0.wireOp",EDGE,"E6.0");Q3=makeQuery(id+"F9.boolean.opBoolean","INTERSECT",EDGE,{"derivedFrom":[makeQuery(id+"F5.opFillet","BLEND_FACE",FACE,{"disambiguationData":[OSD([subQ5,subQ4,subQ3,subQ2,subQ1,subQ0]),TDD([makeQuery(id+"F3.boolean.opBoolean","INTERSECT",EDGE,{"disambiguationData":[OD(0.0)],"derivedFrom":[makeQuery(id+"F1.opExtrude","SWEPT_FACE",FACE,{"disambiguationData":[OSD([subQ5])]}),makeQuery(id+"F3.opExtrude","CAP_FACE",FACE,{"disambiguationData":[OSD([subQ4,subQ3,subQ2,subQ1,subQ0])],"isStart":false})]})])]}),makeQuery(id+"F9.opExtrude","SWEPT_FACE",FACE,{"disambiguationData":[OSD([sQuery(id+"F2.wireOp",EDGE,"E40.MirrorCS")])]})]});}
            var Q4;
            Q4=makeQuery(id+"F9.boolean.opBoolean","INTERSECT",EDGE,{"derivedFrom":[makeQuery(id+"F3.opExtrude","CAP_FACE",FACE,{"disambiguationData":[OSD([sQuery(id+"F2.wireOp",EDGE,"E10"),sQuery(id+"F2.wireOp",EDGE,"E15"),sQuery(id+"F2.wireOp",EDGE,"E17"),sQuery(id+"F2.wireOp",EDGE,"E18"),sQuery(id+"F2.wireOp",EDGE,"E19")])],"isStart":false}),makeQuery(id+"F9.opExtrude","SWEPT_FACE",FACE,{"disambiguationData":[OSD([sQuery(id+"F2.wireOp",EDGE,"E35.MirrorCS")])]})]});
            var Q5;
            Q5=makeQuery(id+"F9.boolean.opBoolean","INTERSECT",EDGE,{"derivedFrom":[makeQuery(id+"F3.opExtrude","CAP_FACE",FACE,{"disambiguationData":[OSD([sQuery(id+"F2.wireOp",EDGE,"E10"),sQuery(id+"F2.wireOp",EDGE,"E15"),sQuery(id+"F2.wireOp",EDGE,"E17"),sQuery(id+"F2.wireOp",EDGE,"E18"),sQuery(id+"F2.wireOp",EDGE,"E19")])],"isStart":false}),makeQuery(id+"F9.opExtrude","SWEPT_FACE",FACE,{"disambiguationData":[OSD([sQuery(id+"F2.wireOp",EDGE,"E36.MirrorCS")])]})]});
            var Q6;
            {var subQ0=sQuery(id+"F2.wireOp",EDGE,"E19");var subQ1=sQuery(id+"F2.wireOp",EDGE,"E18");var subQ2=sQuery(id+"F2.wireOp",EDGE,"E17");var subQ3=sQuery(id+"F2.wireOp",EDGE,"E15");var subQ4=sQuery(id+"F2.wireOp",EDGE,"E10");var subQ5=sQuery(id+"F0.wireOp",EDGE,"E6.0");Q6=makeQuery(id+"F9.boolean.opBoolean","INTERSECT",EDGE,{"derivedFrom":[makeQuery(id+"F5.opFillet","BLEND_FACE",FACE,{"disambiguationData":[OSD([subQ5,subQ4,subQ3,subQ2,subQ1,subQ0]),TDD([makeQuery(id+"F3.boolean.opBoolean","INTERSECT",EDGE,{"disambiguationData":[OD(1.0)],"derivedFrom":[makeQuery(id+"F1.opExtrude","SWEPT_FACE",FACE,{"disambiguationData":[OSD([subQ5])]}),makeQuery(id+"F3.opExtrude","CAP_FACE",FACE,{"disambiguationData":[OSD([subQ4,subQ3,subQ2,subQ1,subQ0])],"isStart":false})]})])]}),makeQuery(id+"F9.opExtrude","SWEPT_FACE",FACE,{"disambiguationData":[OSD([sQuery(id+"F2.wireOp",EDGE,"E36.MirrorCS")])]})]});}
            var Q7;
            Q7=makeQuery(id+"F9.boolean.opBoolean","INTERSECT",EDGE,{"derivedFrom":[makeQuery(id+"F3.opExtrude","CAP_FACE",FACE,{"disambiguationData":[OSD([sQuery(id+"F2.wireOp",EDGE,"E10"),sQuery(id+"F2.wireOp",EDGE,"E15"),sQuery(id+"F2.wireOp",EDGE,"E17"),sQuery(id+"F2.wireOp",EDGE,"E18"),sQuery(id+"F2.wireOp",EDGE,"E19")])],"isStart":false}),makeQuery(id+"F9.opExtrude","SWEPT_FACE",FACE,{"disambiguationData":[OSD([sQuery(id+"F2.wireOp",EDGE,"E40.MirrorCS")])]})]});
            var Q8;
            {var subQ0=sQuery(id+"F2.wireOp",EDGE,"E19");var subQ1=sQuery(id+"F2.wireOp",EDGE,"E18");var subQ2=sQuery(id+"F2.wireOp",EDGE,"E17");var subQ3=sQuery(id+"F2.wireOp",EDGE,"E15");var subQ4=sQuery(id+"F2.wireOp",EDGE,"E10");var subQ5=sQuery(id+"F0.wireOp",EDGE,"E6.0");Q8=makeQuery(id+"F9.boolean.opBoolean","INTERSECT",EDGE,{"derivedFrom":[makeQuery(id+"F5.opFillet","BLEND_FACE",FACE,{"disambiguationData":[OSD([subQ5,subQ4,subQ3,subQ2,subQ1,subQ0]),TDD([makeQuery(id+"F3.boolean.opBoolean","INTERSECT",EDGE,{"disambiguationData":[OD(1.0)],"derivedFrom":[makeQuery(id+"F1.opExtrude","SWEPT_FACE",FACE,{"disambiguationData":[OSD([subQ5])]}),makeQuery(id+"F3.opExtrude","CAP_FACE",FACE,{"disambiguationData":[OSD([subQ4,subQ3,subQ2,subQ1,subQ0])],"isStart":false})]})])]}),makeQuery(id+"F9.opExtrude","SWEPT_FACE",FACE,{"disambiguationData":[OSD([sQuery(id+"F2.wireOp",EDGE,"E37.MirrorCS")])]})]});}
            var Q9;
            Q9=makeQuery(id+"F9.boolean.opBoolean","INTERSECT",EDGE,{"derivedFrom":[makeQuery(id+"F1.opExtrude","SWEPT_FACE",FACE,{"disambiguationData":[OSD([sQuery(id+"F0.wireOp",EDGE,"E6.0")])]}),makeQuery(id+"F9.opExtrude","SWEPT_FACE",FACE,{"disambiguationData":[OSD([sQuery(id+"F2.wireOp",EDGE,"E37.MirrorCS")])]})]});
            var Q10;
            {var subQ0=sQuery(id+"F2.wireOp",EDGE,"E19");var subQ1=sQuery(id+"F2.wireOp",EDGE,"E18");var subQ2=sQuery(id+"F2.wireOp",EDGE,"E17");var subQ3=sQuery(id+"F2.wireOp",EDGE,"E15");var subQ4=sQuery(id+"F2.wireOp",EDGE,"E10");var subQ5=sQuery(id+"F0.wireOp",EDGE,"E6.0");Q10=makeQuery(id+"F9.boolean.opBoolean","INTERSECT",EDGE,{"derivedFrom":[makeQuery(id+"F5.opFillet","BLEND_FACE",FACE,{"disambiguationData":[OSD([subQ5,subQ4,subQ3,subQ2,subQ1,subQ0]),TDD([makeQuery(id+"F3.boolean.opBoolean","INTERSECT",EDGE,{"disambiguationData":[OD(0.0)],"derivedFrom":[makeQuery(id+"F1.opExtrude","SWEPT_FACE",FACE,{"disambiguationData":[OSD([subQ5])]}),makeQuery(id+"F3.opExtrude","CAP_FACE",FACE,{"disambiguationData":[OSD([subQ4,subQ3,subQ2,subQ1,subQ0])],"isStart":false})]})])]}),makeQuery(id+"F9.opExtrude","SWEPT_FACE",FACE,{"disambiguationData":[OSD([sQuery(id+"F2.wireOp",EDGE,"E39.MirrorCS")])]})]});}
            var Q11;
            Q11=makeQuery(id+"F9.boolean.opBoolean","INTERSECT",EDGE,{"derivedFrom":[makeQuery(id+"F1.opExtrude","SWEPT_FACE",FACE,{"disambiguationData":[OSD([sQuery(id+"F0.wireOp",EDGE,"E6.0")])]}),makeQuery(id+"F9.opExtrude","SWEPT_FACE",FACE,{"disambiguationData":[OSD([sQuery(id+"F2.wireOp",EDGE,"E39.MirrorCS")])]})]});
            var Q12;
            Q12=makeQuery(id+"F9.boolean.opBoolean","COPY",EDGE,{"derivedFrom":makeQuery(id+"F9.opExtrude","SWEPT_EDGE",EDGE,{"disambiguationData":[OSD([sQuery(id+"F2.wireOp",EDGE,"E37.MirrorCS"),sQuery(id+"F2.wireOp",EDGE,"E38.MirrorCS")])]})});
            var Q13;
            Q13=makeQuery(id+"F9.boolean.opBoolean","COPY",EDGE,{"derivedFrom":makeQuery(id+"F9.opExtrude","SWEPT_EDGE",EDGE,{"disambiguationData":[OSD([sQuery(id+"F2.wireOp",EDGE,"E38.MirrorCS"),sQuery(id+"F2.wireOp",EDGE,"E39.MirrorCS")])]})});
            var Q14;
            {var subQ0=sQuery(id+"F2.wireOp",EDGE,"E32.MirrorCS");var subQ1=sQuery(id+"F2.wireOp",EDGE,"E31.MirrorCS");var subQ2=sQuery(id+"F2.wireOp",EDGE,"E22.MirrorC");var subQ3=sQuery(id+"F2.wireOp",EDGE,"E21.MirrorCS");var subQ4=sQuery(id+"F2.wireOp",EDGE,"E20.MirrorCS");var subQ5=sQuery(id+"F0.wireOp",EDGE,"E6.1");Q14=makeQuery(id+"F9.boolean.opBoolean","INTERSECT",EDGE,{"derivedFrom":[makeQuery(id+"F5.opFillet","BLEND_FACE",FACE,{"disambiguationData":[OSD([subQ5,subQ4,subQ3,subQ2,subQ1,subQ0]),TDD([makeQuery(id+"F3.boolean.opBoolean","INTERSECT",EDGE,{"disambiguationData":[OD(0.0)],"derivedFrom":[makeQuery(id+"F1.opExtrude","SWEPT_FACE",FACE,{"disambiguationData":[OSD([subQ5])]}),makeQuery(id+"F3.opExtrude","CAP_FACE",FACE,{"disambiguationData":[OSD([subQ4,subQ3,subQ2,subQ1,subQ0])],"isStart":false})]})])]}),makeQuery(id+"F9.opExtrude","SWEPT_FACE",FACE,{"disambiguationData":[OSD([sQuery(id+"F2.wireOp",EDGE,"E34.2")])]})]});}
            var Q15;
            Q15=makeQuery(id+"F9.boolean.opBoolean","INTERSECT",EDGE,{"derivedFrom":[makeQuery(id+"F1.opExtrude","SWEPT_FACE",FACE,{"disambiguationData":[OSD([sQuery(id+"F0.wireOp",EDGE,"E6.1")])]}),makeQuery(id+"F9.opExtrude","SWEPT_FACE",FACE,{"disambiguationData":[OSD([sQuery(id+"F2.wireOp",EDGE,"E34.2")])]})]});
            var Q16;
            Q16=makeQuery(id+"F9.boolean.opBoolean","INTERSECT",EDGE,{"derivedFrom":[makeQuery(id+"F1.opExtrude","SWEPT_FACE",FACE,{"disambiguationData":[OSD([sQuery(id+"F0.wireOp",EDGE,"E6.2")])]}),makeQuery(id+"F9.opExtrude","SWEPT_FACE",FACE,{"disambiguationData":[OSD([sQuery(id+"F2.wireOp",EDGE,"E34.3")])]})]});
            var Q17;
            {var subQ0=sQuery(id+"F2.wireOp",EDGE,"E32.MirrorCS");var subQ1=sQuery(id+"F2.wireOp",EDGE,"E31.MirrorCS");var subQ2=sQuery(id+"F2.wireOp",EDGE,"E22.MirrorC");var subQ3=sQuery(id+"F2.wireOp",EDGE,"E21.MirrorCS");var subQ4=sQuery(id+"F2.wireOp",EDGE,"E20.MirrorCS");var subQ5=sQuery(id+"F0.wireOp",EDGE,"E6.1");Q17=makeQuery(id+"F9.boolean.opBoolean","INTERSECT",EDGE,{"derivedFrom":[makeQuery(id+"F5.opFillet","BLEND_FACE",FACE,{"disambiguationData":[OSD([subQ5,subQ4,subQ3,subQ2,subQ1,subQ0]),TDD([makeQuery(id+"F3.boolean.opBoolean","INTERSECT",EDGE,{"disambiguationData":[OD(1.0)],"derivedFrom":[makeQuery(id+"F1.opExtrude","SWEPT_FACE",FACE,{"disambiguationData":[OSD([subQ5])]}),makeQuery(id+"F3.opExtrude","CAP_FACE",FACE,{"disambiguationData":[OSD([subQ4,subQ3,subQ2,subQ1,subQ0])],"isStart":false})]})])]}),makeQuery(id+"F9.opExtrude","SWEPT_FACE",FACE,{"disambiguationData":[OSD([sQuery(id+"F2.wireOp",EDGE,"E34.4")])]})]});}
            var Q18;
            Q18=makeQuery(id+"F9.boolean.opBoolean","INTERSECT",EDGE,{"derivedFrom":[makeQuery(id+"F3.opExtrude","CAP_FACE",FACE,{"disambiguationData":[OSD([sQuery(id+"F2.wireOp",EDGE,"E20.MirrorCS"),sQuery(id+"F2.wireOp",EDGE,"E21.MirrorCS"),sQuery(id+"F2.wireOp",EDGE,"E22.MirrorC"),sQuery(id+"F2.wireOp",EDGE,"E31.MirrorCS"),sQuery(id+"F2.wireOp",EDGE,"E32.MirrorCS")])],"isStart":false}),makeQuery(id+"F9.opExtrude","SWEPT_FACE",FACE,{"disambiguationData":[OSD([sQuery(id+"F2.wireOp",EDGE,"E34.5")])]})]});
            var Q19;
            Q19=makeQuery(id+"F9.boolean.opBoolean","INTERSECT",EDGE,{"derivedFrom":[makeQuery(id+"F3.opExtrude","CAP_FACE",FACE,{"disambiguationData":[OSD([sQuery(id+"F2.wireOp",EDGE,"E20.MirrorCS"),sQuery(id+"F2.wireOp",EDGE,"E21.MirrorCS"),sQuery(id+"F2.wireOp",EDGE,"E22.MirrorC"),sQuery(id+"F2.wireOp",EDGE,"E31.MirrorCS"),sQuery(id+"F2.wireOp",EDGE,"E32.MirrorCS")])],"isStart":false}),makeQuery(id+"F9.opExtrude","SWEPT_FACE",FACE,{"disambiguationData":[OSD([sQuery(id+"F2.wireOp",EDGE,"E34.0")])]})]});
            var Q20;
            Q20=makeQuery(id+"F9.boolean.opBoolean","INTERSECT",EDGE,{"derivedFrom":[makeQuery(id+"F3.opExtrude","CAP_FACE",FACE,{"disambiguationData":[OSD([sQuery(id+"F2.wireOp",EDGE,"E20.MirrorCS"),sQuery(id+"F2.wireOp",EDGE,"E21.MirrorCS"),sQuery(id+"F2.wireOp",EDGE,"E22.MirrorC"),sQuery(id+"F2.wireOp",EDGE,"E31.MirrorCS"),sQuery(id+"F2.wireOp",EDGE,"E32.MirrorCS")])],"isStart":false}),makeQuery(id+"F9.opExtrude","SWEPT_FACE",FACE,{"disambiguationData":[OSD([sQuery(id+"F2.wireOp",EDGE,"E34.1")])]})]});
            var Q21;
            Q21=makeQuery(id+"F9.boolean.opBoolean","COPY",EDGE,{"derivedFrom":makeQuery(id+"F9.opExtrude","SWEPT_EDGE",EDGE,{"disambiguationData":[OSD([sQuery(id+"F2.wireOp",EDGE,"E34.3"),sQuery(id+"F2.wireOp",EDGE,"E34.4")])]})});
            var Q22;
            Q22=makeQuery(id+"F9.boolean.opBoolean","COPY",EDGE,{"derivedFrom":makeQuery(id+"F9.opExtrude","SWEPT_EDGE",EDGE,{"disambiguationData":[OSD([sQuery(id+"F2.wireOp",EDGE,"E34.2"),sQuery(id+"F2.wireOp",EDGE,"E34.3")])]})});
            fillet(context, id + "F14", {"entities" : qUnion([Q0, Q1, Q2, Q3, Q4, Q5, Q6, Q7, Q8, Q9, Q10, Q11, Q12, Q13, Q14, Q15, Q16, Q17, Q18, Q19, Q20, Q21, Q22]), "radius" : 0.3 * mm, "tangentPropagation" : true, "allowEdgeOverflow" : false});
        }
    });
